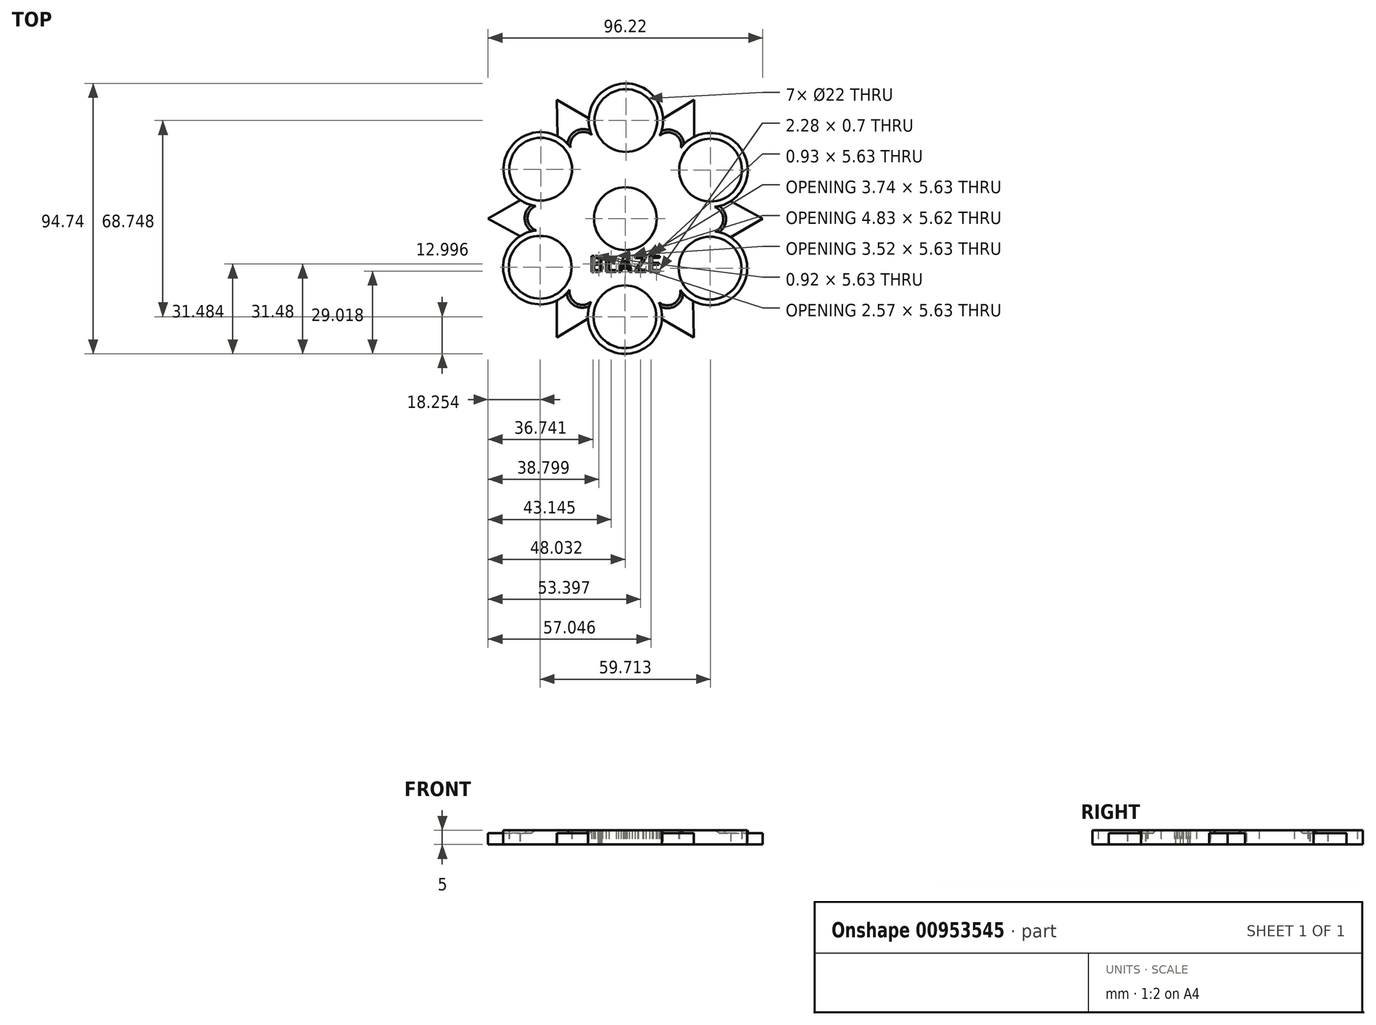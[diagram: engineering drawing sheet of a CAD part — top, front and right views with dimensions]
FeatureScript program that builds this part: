
annotation { "Feature Type Name" : "Feature", "Feature Type Description" : "" }
export const myFeature = defineFeature(function(context is Context, id is Id, definition is map)
    precondition{}
    {
        {
            var Q0;
            Q0=qCreatedBy(makeId("Top.planeOp"),FACE);
            var sketch = newSketch(context, id + "F0", { "sketchPlane" : qUnion([Q0])});
            skCircle(sketch, "E0", {"center": v(0, 0) * mm, "radius": 11 * mm});
            skCircle(sketch, "E1", {"center": v(0.17, 34.37) * mm, "radius": 11 * mm});
            skCircle(sketch, "E2.1.0", {"center": v(-29.68, 17.34) * mm, "radius": 11 * mm});
            skCircle(sketch, "E2.2.0", {"center": v(-29.86, -17.04) * mm, "radius": 11 * mm});
            skCircle(sketch, "E3.1.3.0", {"center": v(-0.17, -34.37) * mm, "radius": 11 * mm});
            skCircle(sketch, "E3.1.4.0", {"center": v(29.68, -17.34) * mm, "radius": 11 * mm});
            skCircle(sketch, "E3.1.5.0", {"center": v(29.86, 17.04) * mm, "radius": 11 * mm});
            skCircle(sketch, "E4", {"center": v(0.17, 34.37) * mm, "radius": 13 * mm});
            skCircle(sketch, "E5.1.0", {"center": v(-29.68, 17.34) * mm, "radius": 13 * mm});
            skCircle(sketch, "E5.2.0", {"center": v(-29.86, -17.04) * mm, "radius": 13 * mm});
            skCircle(sketch, "E5.3.0", {"center": v(-0.17, -34.37) * mm, "radius": 13 * mm});
            skCircle(sketch, "E5.4.0", {"center": v(29.68, -17.34) * mm, "radius": 13 * mm});
            skCircle(sketch, "E5.5.0", {"center": v(29.86, 17.04) * mm, "radius": 13 * mm});
            skArc(sketch, "E6", {"start": v(36.88, -6.52) * mm, "mid": v(39.29, -0.2) * mm, "end": v(36.93, 6.13) * mm});
            skArc(sketch, "E7.1.0", {"start": v(24.09, 28.68) * mm, "mid": v(19.82, 33.92) * mm, "end": v(13.16, 35.04) * mm});
            skArc(sketch, "E7.2.0", {"start": v(-12.8, 35.2) * mm, "mid": v(-19.47, 34.13) * mm, "end": v(-23.77, 28.92) * mm});
            skArc(sketch, "E7.3.0", {"start": v(-36.88, 6.52) * mm, "mid": v(-39.29, 0.2) * mm, "end": v(-36.93, -6.13) * mm});
            skArc(sketch, "E7.4.0", {"start": v(-24.09, -28.68) * mm, "mid": v(-19.82, -33.92) * mm, "end": v(-13.16, -35.04) * mm});
            skArc(sketch, "E7.5.0", {"start": v(12.8, -35.2) * mm, "mid": v(19.47, -34.13) * mm, "end": v(23.77, -28.92) * mm});
            skPoint(sketch, "E8.endSnap0", {"position": v(-19.82, -33.92) * mm});
            skLineSegment(sketch, "E9", {"start": v(-24.09, -28.68) * mm, "end": v(-24.09, -41.65) * mm});
            skLineSegment(sketch, "E10", {"start": v(-24.09, -41.65) * mm, "end": v(-13.16, -35.04) * mm});
            skLineSegment(sketch, "E11.1.0", {"start": v(12.8, -35.2) * mm, "end": v(24.02, -41.68) * mm});
            skLineSegment(sketch, "E11.2.0", {"start": v(36.88, -6.52) * mm, "end": v(48.1, -0.04) * mm});
            skLineSegment(sketch, "E11.3.0", {"start": v(24.09, 28.68) * mm, "end": v(24.09, 41.65) * mm});
            skLineSegment(sketch, "E11.4.0", {"start": v(-12.8, 35.2) * mm, "end": v(-24.02, 41.68) * mm});
            skLineSegment(sketch, "E11.5.0", {"start": v(-36.88, 6.52) * mm, "end": v(-48.1, 0.04) * mm});
            skLineSegment(sketch, "E12.1.0", {"start": v(24.02, -41.68) * mm, "end": v(23.77, -28.92) * mm});
            skLineSegment(sketch, "E12.2.0", {"start": v(48.1, -0.04) * mm, "end": v(36.93, 6.13) * mm});
            skLineSegment(sketch, "E12.3.0", {"start": v(24.09, 41.65) * mm, "end": v(13.16, 35.04) * mm});
            skLineSegment(sketch, "E12.4.0", {"start": v(-24.02, 41.68) * mm, "end": v(-23.77, 28.92) * mm});
            skLineSegment(sketch, "E12.5.0", {"start": v(-48.1, 0.04) * mm, "end": v(-36.93, -6.13) * mm});
            skText(sketch, "E13", { "text": "BLAZE", "fontName": "AllertaStencil-Regular.ttf"});
            const initialGuessF0  = {"E13": [-0.01256, -0.0187, 1, 0, 0.00563]};
            skSetInitialGuess(sketch, initialGuessF0);
            skSolve(sketch);
        }
        {
            var Q0;
            Q0=makeQuery(id+"F0.imprint","IMPRINT",FACE,{"disambiguationData":[TD([[makeQuery(id+"F0.imprint","IMPRINT",EDGE,{"derivedFrom":sQuery(id+"F0.wireOp",EDGE,"E3.1.4.0")}),-1.0]])]});
            var Q1;
            Q1=makeQuery(id+"F0.imprint","IMPRINT",FACE,{"disambiguationData":[TD([[makeQuery(id+"F0.imprint","IMPRINT",EDGE,{"derivedFrom":sQuery(id+"F0.wireOp",EDGE,"E3.1.3.0")}),-1.0]])]});
            var Q2;
            Q2=makeQuery(id+"F0.imprint","IMPRINT",FACE,{"disambiguationData":[TD([[makeQuery(id+"F0.imprint","IMPRINT",EDGE,{"derivedFrom":sQuery(id+"F0.wireOp",EDGE,"E3.1.5.0")}),-1.0]])]});
            var Q3;
            Q3=makeQuery(id+"F0.imprint","IMPRINT",FACE,{"disambiguationData":[TD([[makeQuery(id+"F0.imprint","IMPRINT",EDGE,{"derivedFrom":sQuery(id+"F0.wireOp",EDGE,"E1")}),-1.0]])]});
            var Q4;
            Q4=makeQuery(id+"F0.imprint","IMPRINT",FACE,{"disambiguationData":[TD([[makeQuery(id+"F0.imprint","IMPRINT",EDGE,{"derivedFrom":sQuery(id+"F0.wireOp",EDGE,"E2.1.0")}),-1.0]])]});
            var Q5;
            Q5=makeQuery(id+"F0.imprint","IMPRINT",FACE,{"disambiguationData":[TD([[makeQuery(id+"F0.imprint","IMPRINT",EDGE,{"derivedFrom":sQuery(id+"F0.wireOp",EDGE,"E0")}),-1.0]])]});
            var Q6;
            Q6=makeQuery(id+"F0.imprint","IMPRINT",FACE,{"disambiguationData":[TD([[makeQuery(id+"F0.imprint","IMPRINT",EDGE,{"derivedFrom":sQuery(id+"F0.wireOp",EDGE,"E2.2.0")}),-1.0]])]});
            extrude(context, id + "F1", {"entities" : qUnion([Q0, Q1, Q2, Q3, Q4, Q5, Q6]), "depth" : 5 * mm, "offsetDistance" : 25 * mm});
        }
        {
            var Q0;
            Q0=makeQuery(id+"F0.imprint","IMPRINT",FACE,{"disambiguationData":[TD([[makeQuery(id+"F0.imprint","IMPRINT",EDGE,{"derivedFrom":sQuery(id+"F0.wireOp",EDGE,"E7.4.0")}),-1.0]])]});
            var Q1;
            Q1=makeQuery(id+"F0.imprint","IMPRINT",FACE,{"disambiguationData":[TD([[makeQuery(id+"F0.imprint","IMPRINT",EDGE,{"derivedFrom":sQuery(id+"F0.wireOp",EDGE,"E7.3.0")}),-1.0]])]});
            var Q2;
            Q2=makeQuery(id+"F0.imprint","IMPRINT",FACE,{"disambiguationData":[TD([[makeQuery(id+"F0.imprint","IMPRINT",EDGE,{"derivedFrom":sQuery(id+"F0.wireOp",EDGE,"E7.2.0")}),-1.0]])]});
            var Q3;
            Q3=makeQuery(id+"F0.imprint","IMPRINT",FACE,{"disambiguationData":[TD([[makeQuery(id+"F0.imprint","IMPRINT",EDGE,{"derivedFrom":sQuery(id+"F0.wireOp",EDGE,"E7.1.0")}),-1.0]])]});
            var Q4;
            Q4=makeQuery(id+"F0.imprint","IMPRINT",FACE,{"disambiguationData":[TD([[makeQuery(id+"F0.imprint","IMPRINT",EDGE,{"derivedFrom":sQuery(id+"F0.wireOp",EDGE,"E6")}),-1.0]])]});
            var Q5;
            Q5=makeQuery(id+"F0.imprint","IMPRINT",FACE,{"disambiguationData":[TD([[makeQuery(id+"F0.imprint","IMPRINT",EDGE,{"derivedFrom":sQuery(id+"F0.wireOp",EDGE,"E7.5.0")}),-1.0]])]});
            extrude(context, id + "F2", {"entities" : qUnion([Q0, Q1, Q2, Q3, Q4, Q5]), "operationType" : NewBodyOperationType.ADD, "depth" : 4 * mm, "offsetDistance" : 25 * mm});
        }
        {
            var Q0;
            Q0=makeQuery(id+"F1.opExtrude","CAP_EDGE",EDGE,{"disambiguationData":[OSD([sQuery(id+"F0.wireOp",EDGE,"E7.4.0")])],"isStart":false});
            var Q1;
            Q1=makeQuery(id+"F1.opExtrude","CAP_EDGE",EDGE,{"disambiguationData":[OSD([sQuery(id+"F0.wireOp",EDGE,"E7.3.0")])],"isStart":false});
            var Q2;
            Q2=makeQuery(id+"F1.opExtrude","CAP_EDGE",EDGE,{"disambiguationData":[OSD([sQuery(id+"F0.wireOp",EDGE,"E7.2.0")])],"isStart":false});
            var Q3;
            Q3=makeQuery(id+"F1.opExtrude","CAP_EDGE",EDGE,{"disambiguationData":[OSD([sQuery(id+"F0.wireOp",EDGE,"E7.1.0")])],"isStart":false});
            var Q4;
            Q4=makeQuery(id+"F1.opExtrude","CAP_EDGE",EDGE,{"disambiguationData":[OSD([sQuery(id+"F0.wireOp",EDGE,"E6")])],"isStart":false});
            var Q5;
            Q5=makeQuery(id+"F1.opExtrude","CAP_EDGE",EDGE,{"disambiguationData":[OSD([sQuery(id+"F0.wireOp",EDGE,"E7.5.0")])],"isStart":false});
            chamfer(context, id + "F3", {"entities" : qUnion([Q0, Q1, Q2, Q3, Q4, Q5]), "width" : 5 * mm, "tangentPropagation" : true});
        }
    });
